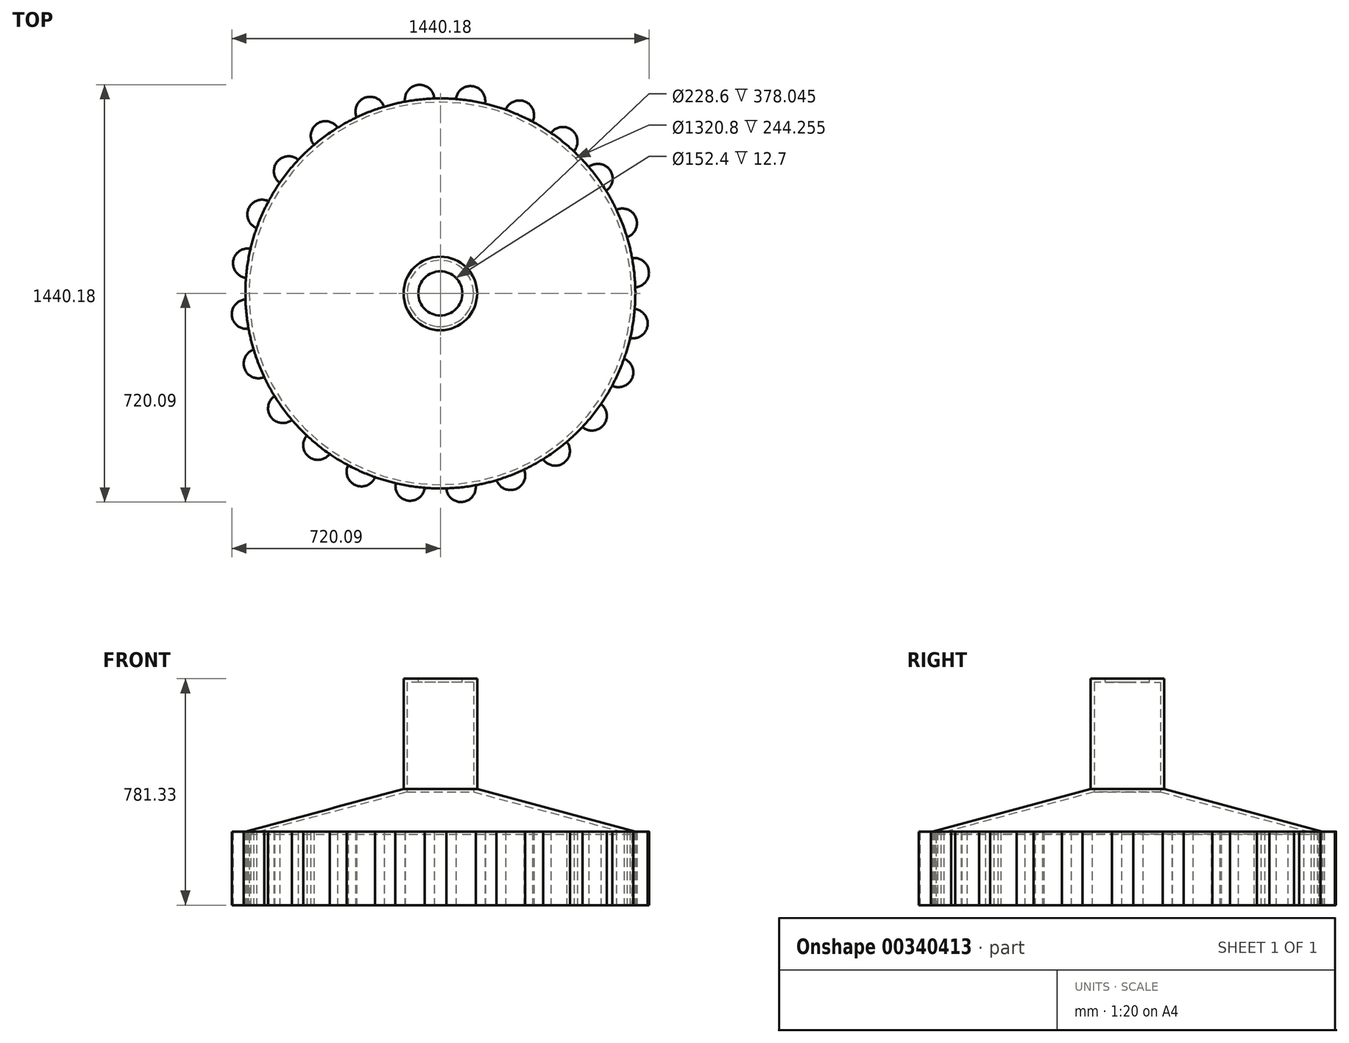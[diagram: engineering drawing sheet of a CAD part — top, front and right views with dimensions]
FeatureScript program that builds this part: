
annotation { "Feature Type Name" : "Feature", "Feature Type Description" : "" }
export const myFeature = defineFeature(function(context is Context, id is Id, definition is map)
    precondition{}
    {
        {
            var Q0;
            Q0=qCreatedBy(makeId("Front.planeOp"),FACE);
            var sketch = newSketch(context, id + "F0", { "sketchPlane" : qUnion([Q0])});
            skLineSegment(sketch, "E0", {"start": v(0, 0) * mm, "end": v(-673.1, 0) * mm});
            skLineSegment(sketch, "E1", {"start": v(-673.1, 0) * mm, "end": v(-673.1, 254) * mm});
            skLineSegment(sketch, "E2", {"start": v(-673.1, 254) * mm, "end": v(-127, 400.33) * mm});
            skPoint(sketch, "E3.center", {"position": v(0, 0) * mm});
            skLineSegment(sketch, "E4", {"start": v(0, 0) * mm, "end": v(0, 1146.38) * mm, "construction": true});
            skLineSegment(sketch, "E5", {"start": v(0, 0) * mm, "end": v(0, 781.33) * mm});
            skLineSegment(sketch, "E6", {"start": v(-127, 781.33) * mm, "end": v(0, 781.33) * mm});
            skLineSegment(sketch, "E7", {"start": v(-127, 400.33) * mm, "end": v(-127, 781.33) * mm});
            skSolve(sketch);
        }
        {
            var Q0;
            Q0=makeQuery(id+"F0.imprint","IMPRINT",FACE,{"disambiguationData":[TD([[makeQuery(id+"F0.imprint","IMPRINT",EDGE,{"derivedFrom":sQuery(id+"F0.wireOp",EDGE,"E0")}),-1.0]])]});
            var Q1;
            Q1=sQuery(id+"F0.wireOp",EDGE,"E4");
            revolve(context, id + "F1", {"entities" : qUnion([Q0]), "axis" : qUnion([Q1]), "revolveType" : RevolveType.FULL});
        }
        {
            var Q0;
            Q0=makeQuery(id+"F1.opRevolve","SWEPT_FACE",FACE,{"disambiguationData":[OSD([sQuery(id+"F0.wireOp",EDGE,"E0")])]});
            shell(context, id + "F2", {"entities" : qUnion([Q0]), "thickness" : 12.7 * mm});
        }
        {
            var Q0;
            Q0=makeQuery(id+"F1.opRevolve","SWEPT_FACE",FACE,{"disambiguationData":[OSD([sQuery(id+"F0.wireOp",EDGE,"E6")])]});
            var sketch = newSketch(context, id + "F3", { "sketchPlane" : qUnion([Q0])});
            skCircle(sketch, "E8", {"center": v(0, 0) * mm, "radius": 76.2 * mm});
            skSolve(sketch);
        }
        {
            var Q0;
            Q0 = qSketchRegion(id + "F3", true);
            extrude(context, id + "F4", {"entities" : qUnion([Q0]), "operationType" : NewBodyOperationType.REMOVE, "endBound" : BoundingType.THROUGH_ALL, "oppositeDirection" : true, "depth" : 25.4 * mm});
        }
        {
            var Q0;
            Q0=makeQuery(id+"F1.opRevolve","SWEPT_FACE",FACE,{"disambiguationData":[OSD([sQuery(id+"F0.wireOp",EDGE,"E0")])]});
            var sketch = newSketch(context, id + "F5", { "sketchPlane" : qUnion([Q0])});
            skArc(sketch, "E9", {"start": v(-607.93, 288.94) * mm, "mid": v(-675.38, 260.55) * mm, "end": v(-644.47, 194.22) * mm});
            skArc(sketch, "E10", {"start": v(-607.93, 288.94) * mm, "mid": v(-627.99, 242.27) * mm, "end": v(-644.47, 194.22) * mm});
            skSolve(sketch);
        }
        {
            var Q0;
            Q0=makeQuery(id+"F5.imprint","IMPRINT",FACE,{"disambiguationData":[TD([[makeQuery(id+"F5.imprint","IMPRINT",EDGE,{"derivedFrom":sQuery(id+"F5.wireOp",EDGE,"E9")}),1.0]])]});
            extrude(context, id + "F6", {"entities" : qUnion([Q0]), "oppositeDirection" : true, "depth" : 254 * mm});
        }
        {
            var Q0;
            Q0=makeQuery(id+"F6.opExtrude","SWEPT_BODY",BODY,{"disambiguationData":[OSD([sQuery(id+"F5.wireOp",EDGE,"E9"),sQuery(id+"F5.wireOp",EDGE,"E10")])]});
            var Q1;
            Q1=makeQuery(id+"F4.boolean.opBoolean","INTERSECT",EDGE,{"derivedFrom":[makeQuery(id+"F2.opShell","OFFSET_FACE",FACE,{"disambiguationData":[OSD([sQuery(id+"F0.wireOp",EDGE,"E6")])]}),makeQuery(id+"F4.opExtrude","SWEPT_FACE",FACE,{"disambiguationData":[OSD([sQuery(id+"F3.wireOp",EDGE,"E8")])]})]});
            circularPattern(context, id + "F7", {"operationType" : NewBodyOperationType.ADD, "entities" : qUnion([Q0]), "axis" : qUnion([Q1]), "angle" : 360 * degree, "instanceCount" : 24, "equalSpace" : true});
        }
    });
